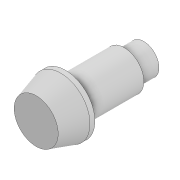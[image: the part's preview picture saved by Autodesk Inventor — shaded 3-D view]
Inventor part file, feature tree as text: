
AUTODESK INVENTOR PART (.ipt)
format: ipt  version: 2022 (Build 260153000, 153)  size: 106,496 bytes
history: native  units: mm
features: sketch x5, extrude x3, plane x1, loft x1, projected_geometry x1
ambient origin geometry x8: Origin, YZ Plane, XZ Plane, XY Plane, X Axis, Y Axis, Z Axis, Center Point
bodies: Solid1 (feature_tree)
feature tree (11):
  sketch  "Sketch2"  dims[d0=12.0mm d1=5.0mm]
  plane  "Work Plane1"
  loft  "Loft1"
  extrude  "Extrusion1"  TaperAngle=0.0deg  [1 undecoded]
  extrude  "Extrusion2"  Depth=1.0mm TaperAngle=0.0deg
  extrude  "Extrusion3"  Depth=12.0mm TaperAngle=0.0deg
  sketch  "Sketch3"  dims[d2=9.0mm d3=0.0mm d4=90.0deg]
  sketch  "Sketch4"  dims[d5=0.0mm d6=90.0deg d7=1.0mm d8=0.0mm]
  sketch  "Sketch5"  dims[d9=8.0mm d10=12.0mm d11=0.0mm]
  sketch  "Sketch6"  dims[d12=6.2mm d13=4.0mm d14=0.0mm]
  projected_geometry  "Project Cut Edges1"
note: 1 required parameter value undecoded (feature->parameter linkage not recoverable at this tier; creation-order binding heuristic only, values carry confidence <= 0.55)
